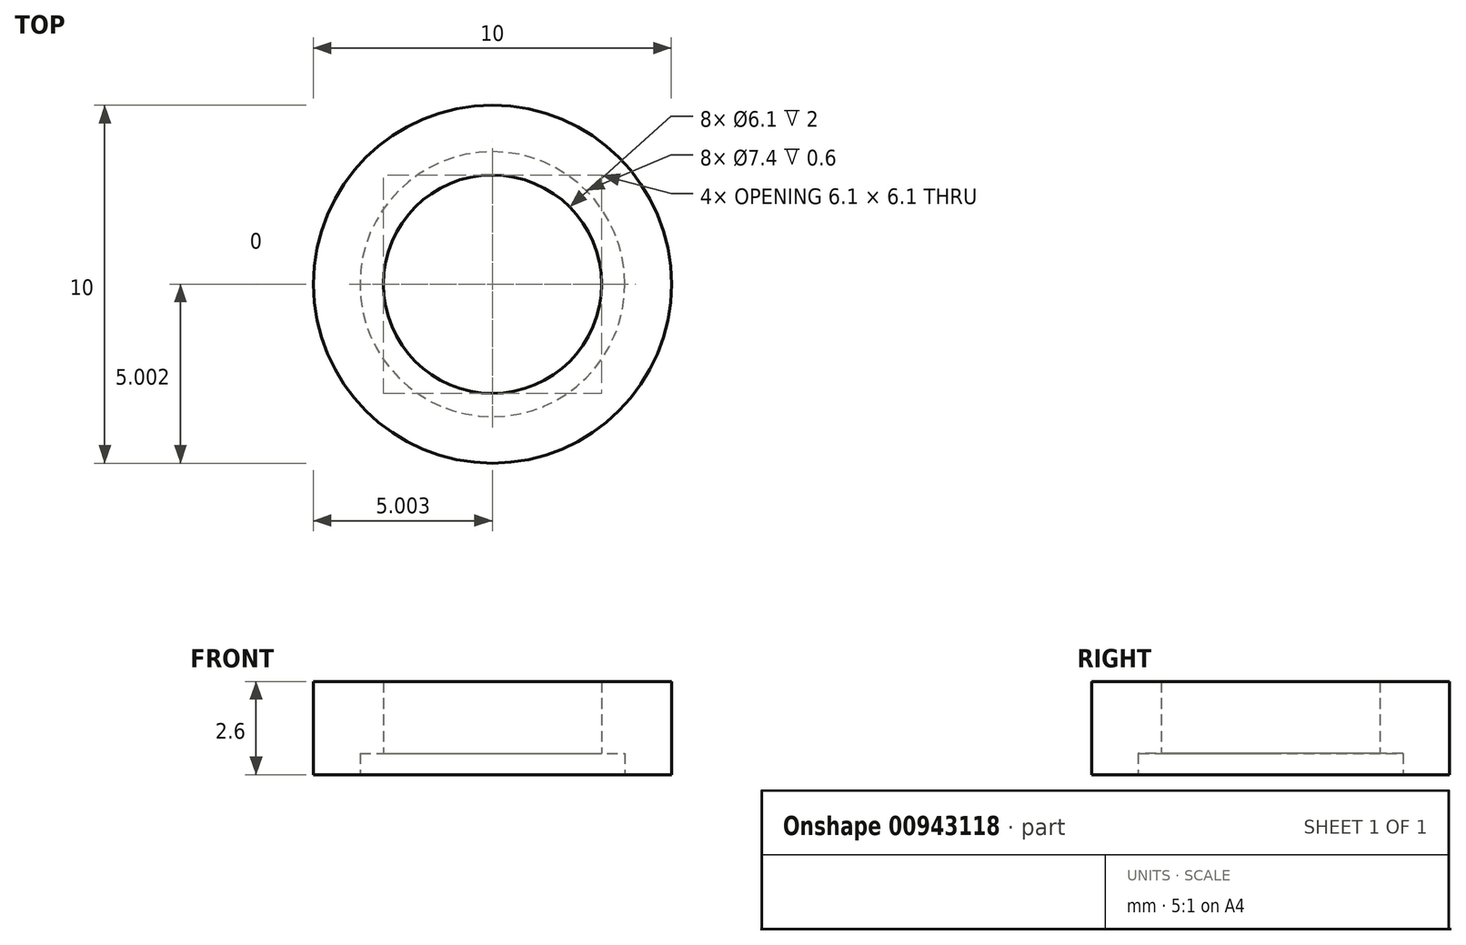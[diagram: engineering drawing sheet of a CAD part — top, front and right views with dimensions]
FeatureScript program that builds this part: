
annotation { "Feature Type Name" : "Feature", "Feature Type Description" : "" }
export const myFeature = defineFeature(function(context is Context, id is Id, definition is map)
    precondition{}
    {
        {
            var Q0;
            Q0=qCreatedBy(makeId("Top.planeOp"),FACE);
            var sketch = newSketch(context, id + "F0", { "sketchPlane" : qUnion([Q0])});
            skCircle(sketch, "E0", {"center": v(-4.42, 6.83) * mm, "radius": 5 * mm});
            skSolve(sketch);
        }
        {
            var Q0;
            Q0=qSketchRegion(id+"F0",true);
            extrude(context, id + "F1", {"entities" : qUnion([Q0]), "depth" : 2.6 * mm, "offsetDistance" : 25 * mm});
        }
        {
            var Q0;
            Q0=sQuery(id+"F0.wireOp",VERTEX,"E0.center");
            var Q1;
            Q1=makeQuery(id+"F1.opExtrude","SWEPT_BODY",BODY,{"disambiguationData":[OSD([sQuery(id+"F0.wireOp",EDGE,"E0")])]});
            hole(context, id + "F2", {"style" : HoleStyle.C_BORE, "endStyle" : HoleEndStyle.BLIND, "oppositeDirection" : true, "holeDiameter" : 6.1 * mm, "cBoreDiameter" : 7.4 * mm, "cBoreDepth" : 0.6 * mm, "majorDiameter" : 5 * mm, "holeDepth" : 3 * mm, "isTappedThrough" : true, "tappedDepth" : 12 * mm, "tapClearance" : 3, "startFromSketch" : true, "locations" : qUnion([Q0]), "scope" : qUnion([Q1])});
        }
    });
